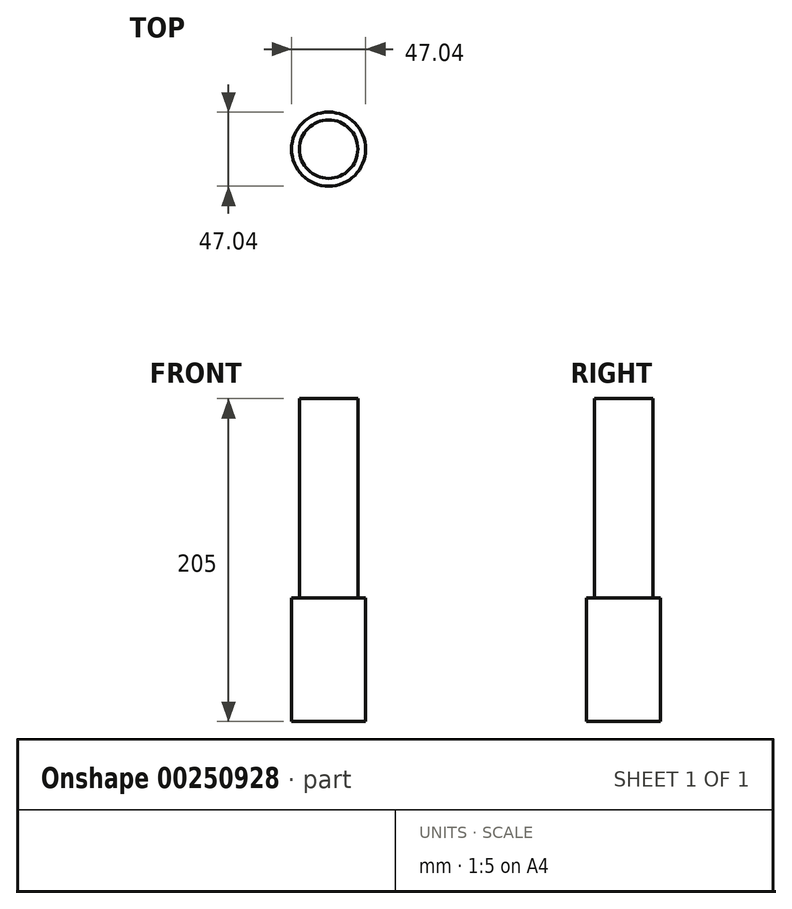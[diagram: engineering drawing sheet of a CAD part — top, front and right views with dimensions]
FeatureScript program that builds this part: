
annotation { "Feature Type Name" : "Feature", "Feature Type Description" : "" }
export const myFeature = defineFeature(function(context is Context, id is Id, definition is map)
    precondition{}
    {
        {
            var Q0;
            Q0=qCreatedBy(makeId("Front.planeOp"),FACE);
            var sketch = newSketch(context, id + "F0", { "sketchPlane" : qUnion([Q0])});
            skLineSegment(sketch, "E0.bottom", {"start": v(23.52, -39.16) * mm, "end": v(-23.52, -39.16) * mm});
            skLineSegment(sketch, "E0.top", {"start": v(23.52, 39.16) * mm, "end": v(-23.52, 39.16) * mm});
            skLineSegment(sketch, "E0.left", {"start": v(23.52, -39.16) * mm, "end": v(23.52, 39.16) * mm});
            skLineSegment(sketch, "E0.right", {"start": v(-23.52, -39.16) * mm, "end": v(-23.52, 39.16) * mm});
            skPoint(sketch, "E0.middle", {"position": v(0, 0) * mm});
            skLineSegment(sketch, "E1", {"start": v(0, 39.16) * mm, "end": v(0, -39.16) * mm});
            skSolve(sketch);
        }
        {
            var Q0;
            {var subQ0=sQuery(id+"F0.wireOp",EDGE,"E0.right");Q0=makeQuery(id+"F0.imprint","IMPRINT",FACE,{"disambiguationData":[TD([[makeQuery(id+"F0.imprint","IMPRINT",EDGE,{"derivedFrom":subQ0}),-1.0]])]});}
            var Q1;
            Q1=sQuery(id+"F0.wireOp",EDGE,"E1");
            revolve(context, id + "F1", {"entities" : qUnion([Q0]), "axis" : qUnion([Q1]), "revolveType" : RevolveType.FULL});
        }
        {
            var Q0;
            Q0=makeQuery(id+"F1.opRevolve","SWEPT_FACE",FACE,{"disambiguationData":[OSD([sQuery(id+"F0.wireOp",EDGE,"E0.top")])]});
            shell(context, id + "F2", {"entities" : qUnion([Q0]), "thickness" : 5 * mm});
        }
        {
            var Q0;
            Q0=makeQuery(id+"F2.opShell","OFFSET_FACE",FACE,{"disambiguationData":[OSD([sQuery(id+"F0.wireOp",EDGE,"E0.bottom")])]});
            extrude(context, id + "F3", {"entities" : qUnion([Q0]), "operationType" : NewBodyOperationType.ADD, "depth" : 200 * mm});
        }
    });
